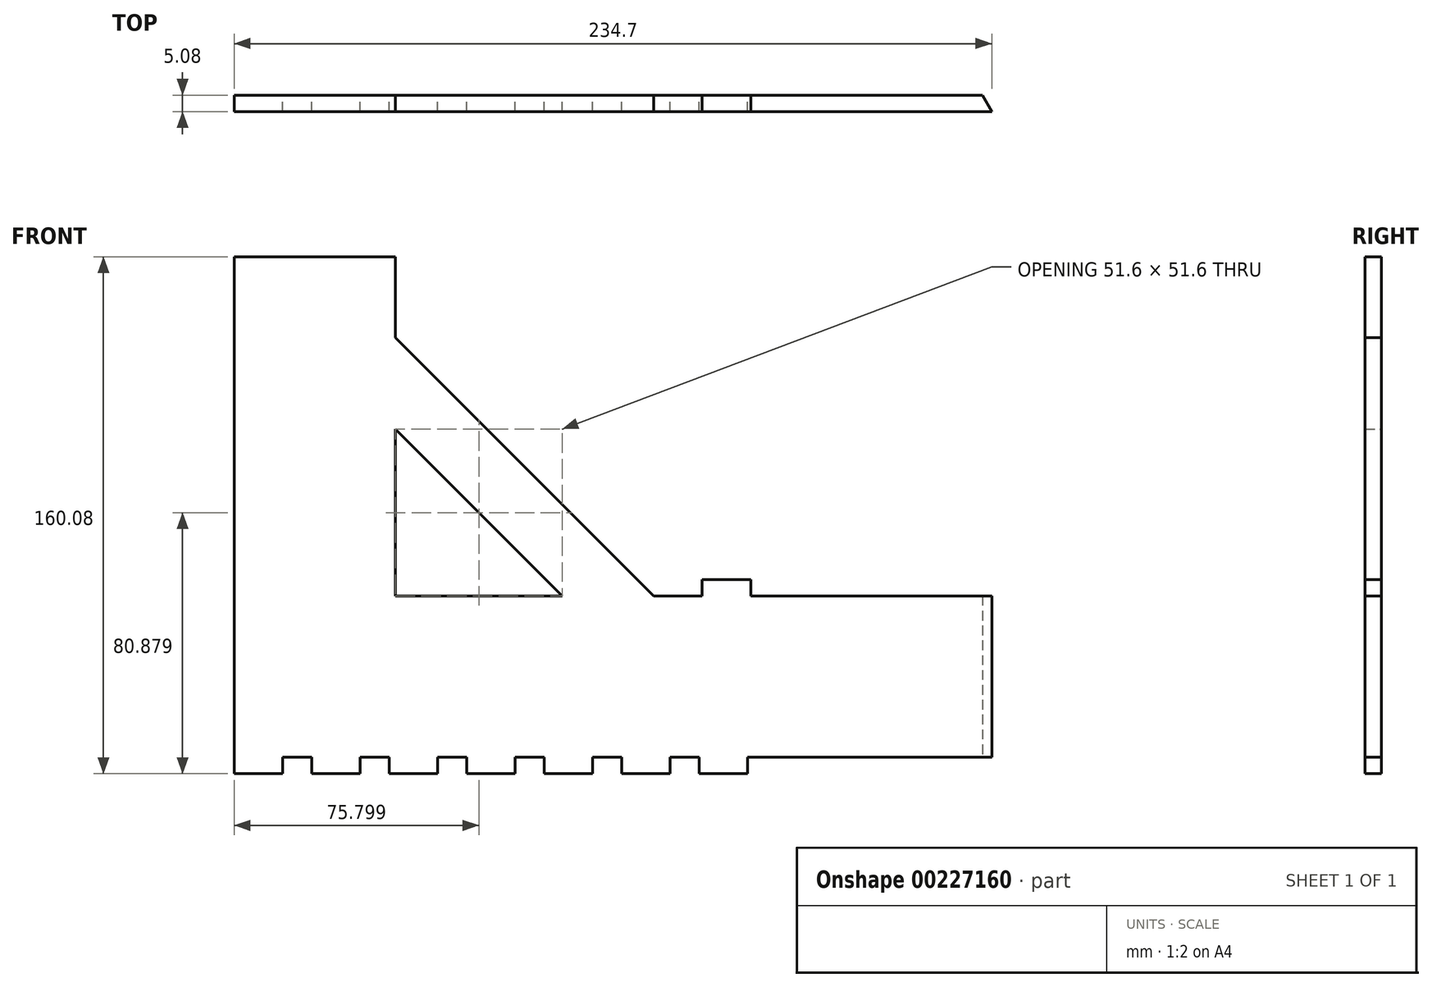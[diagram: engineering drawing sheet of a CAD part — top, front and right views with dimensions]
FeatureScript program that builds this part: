
annotation { "Feature Type Name" : "Feature", "Feature Type Description" : "" }
export const myFeature = defineFeature(function(context is Context, id is Id, definition is map)
    precondition{}
    {
        {
            var Q0;
            Q0=qCreatedBy(makeId("Front.planeOp"),FACE);
            var sketch = newSketch(context, id + "F0", { "sketchPlane" : qUnion([Q0])});
            skLineSegment(sketch, "E0", {"start": v(0, 0) * mm, "end": v(-234.7, 0) * mm});
            skLineSegment(sketch, "E1", {"start": v(-234.7, 0) * mm, "end": v(-234.7, 130) * mm});
            skLineSegment(sketch, "E2", {"start": v(-234.7, 130) * mm, "end": v(-184.7, 130) * mm});
            skLineSegment(sketch, "E3", {"start": v(-184.7, 130) * mm, "end": v(-184.7, 50) * mm});
            skLineSegment(sketch, "E4", {"start": v(-184.7, 50) * mm, "end": v(0, 50) * mm});
            skLineSegment(sketch, "E5", {"start": v(-184.7, 130) * mm, "end": v(-104.7, 50) * mm});
            skLineSegment(sketch, "E6", {"start": v(-184.7, 101.6) * mm, "end": v(-133.1, 50) * mm});
            skLineSegment(sketch, "E7", {"start": v(-234.7, 0) * mm, "end": v(-234.7, -5.08) * mm});
            skLineSegment(sketch, "E8", {"start": v(-234.7, -5.08) * mm, "end": v(-219.7, -5.08) * mm});
            skLineSegment(sketch, "E9", {"start": v(-219.7, -5.08) * mm, "end": v(-219.7, 0) * mm});
            skLineSegment(sketch, "E10.1.0.0", {"start": v(-195.7, -5.08) * mm, "end": v(-195.7, 0) * mm});
            skLineSegment(sketch, "E10.1.0.1", {"start": v(-210.7, -5.08) * mm, "end": v(-195.7, -5.08) * mm});
            skLineSegment(sketch, "E10.1.0.2", {"start": v(-210.7, 0) * mm, "end": v(-210.7, -5.08) * mm});
            skLineSegment(sketch, "E10.2.0.0", {"start": v(-171.7, -5.08) * mm, "end": v(-171.7, 0) * mm});
            skLineSegment(sketch, "E10.2.0.1", {"start": v(-186.7, -5.08) * mm, "end": v(-171.7, -5.08) * mm});
            skLineSegment(sketch, "E10.2.0.2", {"start": v(-186.7, 0) * mm, "end": v(-186.7, -5.08) * mm});
            skLineSegment(sketch, "E10.3.0.0", {"start": v(-147.7, -5.08) * mm, "end": v(-147.7, 0) * mm});
            skLineSegment(sketch, "E10.3.0.1", {"start": v(-162.7, -5.08) * mm, "end": v(-147.7, -5.08) * mm});
            skLineSegment(sketch, "E10.3.0.2", {"start": v(-162.7, 0) * mm, "end": v(-162.7, -5.08) * mm});
            skLineSegment(sketch, "E10.4.0.0", {"start": v(-123.7, -5.08) * mm, "end": v(-123.7, 0) * mm});
            skLineSegment(sketch, "E10.4.0.1", {"start": v(-138.7, -5.08) * mm, "end": v(-123.7, -5.08) * mm});
            skLineSegment(sketch, "E10.4.0.2", {"start": v(-138.7, 0) * mm, "end": v(-138.7, -5.08) * mm});
            skLineSegment(sketch, "E10.5.0.0", {"start": v(-99.7, -5.08) * mm, "end": v(-99.7, 0) * mm});
            skLineSegment(sketch, "E10.5.0.1", {"start": v(-114.7, -5.08) * mm, "end": v(-99.7, -5.08) * mm});
            skLineSegment(sketch, "E10.5.0.2", {"start": v(-114.7, 0) * mm, "end": v(-114.7, -5.08) * mm});
            skLineSegment(sketch, "E10.6.0.0", {"start": v(-75.7, -5.08) * mm, "end": v(-75.7, 0) * mm});
            skLineSegment(sketch, "E10.6.0.1", {"start": v(-90.7, -5.08) * mm, "end": v(-75.7, -5.08) * mm});
            skLineSegment(sketch, "E10.6.0.2", {"start": v(-90.7, 0) * mm, "end": v(-90.7, -5.08) * mm});
            skLineSegment(sketch, "E10.direction1", {"start": v(-234.7, -5.08) * mm, "end": v(-210.7, -5.08) * mm, "construction": true});
            skLineSegment(sketch, "E11", {"start": v(0, 50) * mm, "end": v(0, 0) * mm});
            skSolve(sketch);
        }
        {
            var Q0;
            Q0=qSketchRegion(id+"F0",true);
            extrude(context, id + "F1", {"entities" : qUnion([Q0]), "depth" : 5.08 * mm});
        }
        {
            var Q0;
            Q0=makeQuery(id+"F1.opExtrude","SWEPT_FACE",FACE,{"disambiguationData":[OSD([sQuery(id+"F0.wireOp",EDGE,"E2")])]});
            var Q1;
            Q1=makeQuery(id+"F1.opExtrude","SWEPT_FACE",FACE,{"disambiguationData":[OSD([sQuery(id+"F0.wireOp",EDGE,"0f3f7d79-0024-4810-854d-b7a6c9fa19c64.MirrorCS")])]});
            extrude(context, id + "F2", {"entities" : qUnion([Q0, Q1]), "operationType" : NewBodyOperationType.ADD, "depth" : 25 * mm});
        }
        {
            var Q0;
            {var subQ0=sQuery(id+"F0.wireOp",EDGE,"E0");Q0=makeQuery(id+"F1.opExtrude","SWEPT_FACE",FACE,{"disambiguationData":[OSD([subQ0]),TDD([makeQuery(id+"F0.imprint","IMPRINT",EDGE,{"disambiguationData":[TD([[makeQuery(id+"F0.imprint","INTERSECT",VERTEX,{"derivedFrom":[subQ0,sQuery(id+"F0.wireOp",EDGE,"E11")]}),-1.0]])],"derivedFrom":subQ0})])]});}
            var sketch = newSketch(context, id + "F3", { "sketchPlane" : qUnion([Q0])});
            skLineSegment(sketch, "E12", {"start": v(0, 5.08) * mm, "end": v(-2.93, 0) * mm});
            skPoint(sketch, "E13.end.orphan", {"position": v(-2.93, 5.08) * mm});
            skSolve(sketch);
        }
        {
            var Q0;
            {var subQ0=sQuery(id+"F3.wireOp",EDGE,"E12");Q0=makeQuery(id+"F3.imprint","IMPRINT",FACE,{"disambiguationData":[TD([[makeQuery(id+"F3.imprint","IMPRINT",EDGE,{"derivedFrom":subQ0}),1.0]])]});}
            extrude(context, id + "F4", {"entities" : qUnion([Q0]), "operationType" : NewBodyOperationType.REMOVE, "oppositeDirection" : true, "depth" : 50 * mm});
        }
        {
            var Q0;
            {var subQ0=sQuery(id+"F0.wireOp",EDGE,"E4");Q0=makeQuery(id+"F1.opExtrude","SWEPT_FACE",FACE,{"disambiguationData":[OSD([subQ0]),TDD([makeQuery(id+"F0.imprint","IMPRINT",EDGE,{"disambiguationData":[TD([[makeQuery(id+"F0.imprint","INTERSECT",VERTEX,{"derivedFrom":[subQ0,sQuery(id+"F0.wireOp",EDGE,"E11")]}),1.0]])],"derivedFrom":subQ0})])]});}
            var sketch = newSketch(context, id + "F5", { "sketchPlane" : qUnion([Q0])});
            skLineSegment(sketch, "E14.bottom", {"start": v(-89.7, 0) * mm, "end": v(-74.7, 0) * mm});
            skLineSegment(sketch, "E14.top", {"start": v(-89.7, -5.08) * mm, "end": v(-74.7, -5.08) * mm});
            skLineSegment(sketch, "E14.right", {"start": v(-74.7, 0) * mm, "end": v(-74.7, -5.08) * mm});
            skLineSegment(sketch, "E15", {"start": v(-89.7, 0) * mm, "end": v(-89.7, -5.08) * mm});
            skPoint(sketch, "E14.left.start.orphan", {"position": v(-104.7, 0) * mm});
            skPoint(sketch, "E16.orphan", {"position": v(-104.7, -5.08) * mm});
            skSolve(sketch);
        }
        {
            var Q0;
            Q0=makeQuery(id+"F5.imprint","IMPRINT",FACE,{"disambiguationData":[TD([[makeQuery(id+"F5.imprint","IMPRINT",EDGE,{"derivedFrom":sQuery(id+"F5.wireOp",EDGE,"E14.bottom")}),-1.0]])]});
            extrude(context, id + "F6", {"entities" : qUnion([Q0]), "operationType" : NewBodyOperationType.ADD, "depth" : 5.08 * mm});
        }
    });
